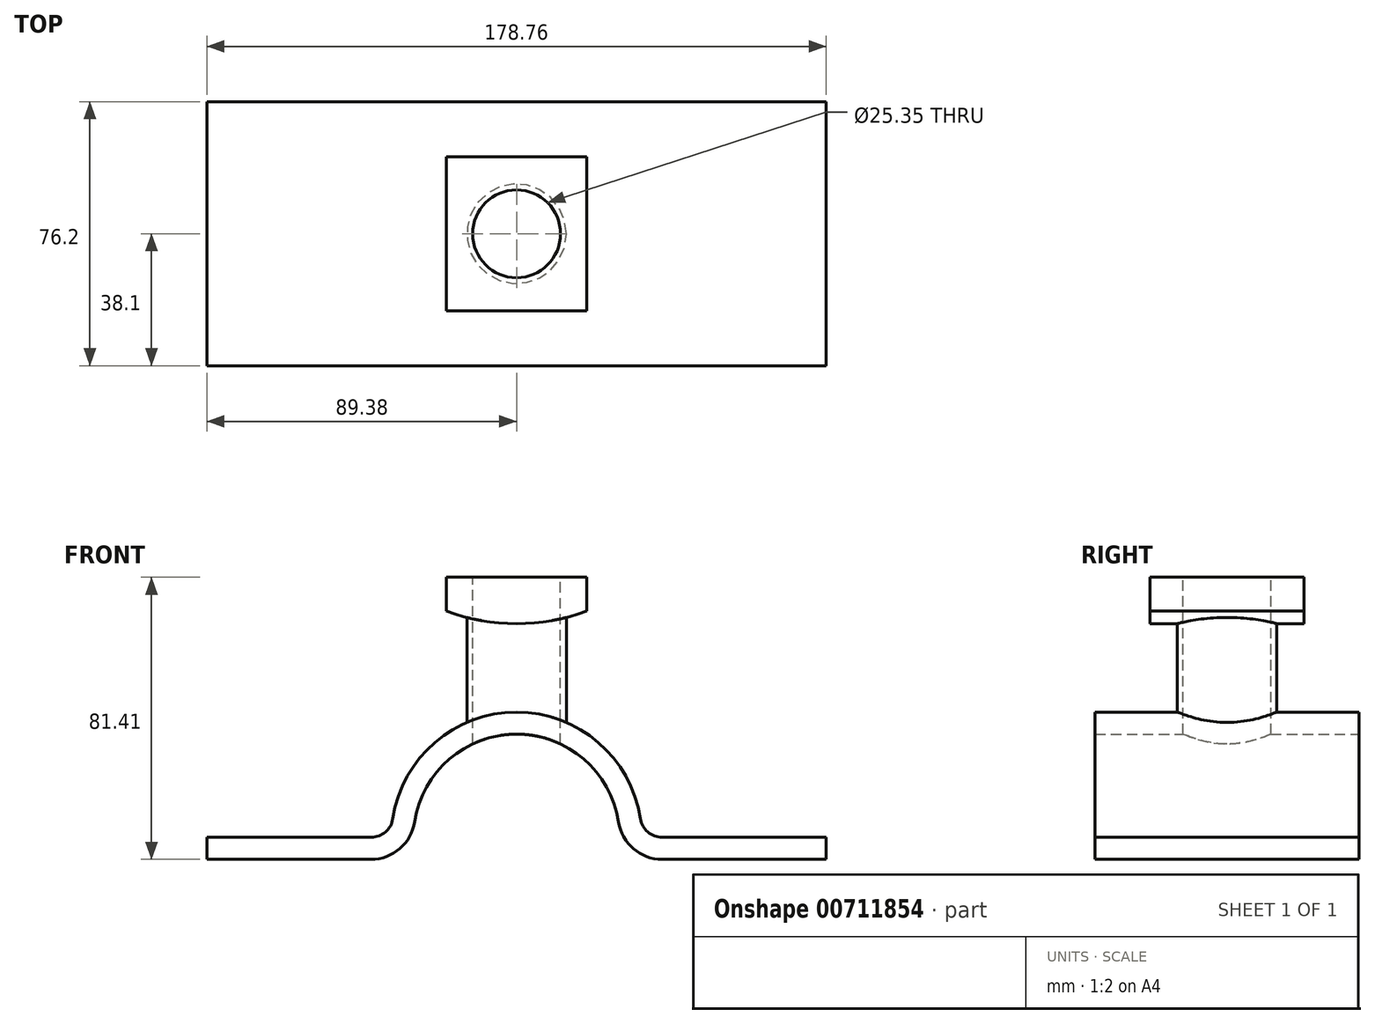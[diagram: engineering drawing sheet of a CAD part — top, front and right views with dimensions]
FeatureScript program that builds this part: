
annotation { "Feature Type Name" : "Feature", "Feature Type Description" : "" }
export const myFeature = defineFeature(function(context is Context, id is Id, definition is map)
    precondition{}
    {
        {
            var Q0;
            Q0=qCreatedBy(makeId("Front.planeOp"),FACE);
            var sketch = newSketch(context, id + "F0", { "sketchPlane" : qUnion([Q0])});
            skArc(sketch, "E0", {"start": v(35.71, 5.4) * mm, "mid": v(0, 36.12) * mm, "end": v(-35.71, 5.4) * mm});
            skLineSegment(sketch, "E1", {"start": v(42, 0) * mm, "end": v(89.38, 0) * mm});
            skLineSegment(sketch, "E2.MirrorCS", {"start": v(-42, 0) * mm, "end": v(-89.38, 0) * mm});
            skPoint(sketch, "E3.visualSharp", {"position": v(-36.12, 0) * mm});
            skArc(sketch, "E3.filletArc", {"start": v(-42, 0) * mm, "mid": v(-37.85, 1.54) * mm, "end": v(-35.71, 5.4) * mm});
            skPoint(sketch, "E4.visualSharp", {"position": v(36.12, 0) * mm});
            skArc(sketch, "E4.filletArc", {"start": v(35.71, 5.4) * mm, "mid": v(37.85, 1.54) * mm, "end": v(42, 0) * mm});
            skLineSegment(sketch, "E5.0", {"start": v(-42, -6.35) * mm, "end": v(-89.38, -6.35) * mm});
            skLineSegment(sketch, "E5.1", {"start": v(42, -6.35) * mm, "end": v(89.38, -6.35) * mm});
            skArc(sketch, "E5.2", {"start": v(29.43, 4.45) * mm, "mid": v(33.7, -3.28) * mm, "end": v(42, -6.35) * mm});
            skArc(sketch, "E5.3", {"start": v(29.43, 4.45) * mm, "mid": v(0, 29.77) * mm, "end": v(-29.43, 4.45) * mm});
            skArc(sketch, "E5.4", {"start": v(-42, -6.35) * mm, "mid": v(-33.7, -3.28) * mm, "end": v(-29.43, 4.45) * mm});
            skLineSegment(sketch, "E6", {"start": v(-89.38, 0) * mm, "end": v(-89.38, -6.35) * mm});
            skLineSegment(sketch, "E7", {"start": v(89.38, 0) * mm, "end": v(89.38, -6.35) * mm});
            skSolve(sketch);
        }
        {
            var Q0;
            Q0=makeQuery(id+"F0.imprint","IMPRINT",FACE,{"disambiguationData":[TD([[makeQuery(id+"F0.imprint","IMPRINT",EDGE,{"derivedFrom":sQuery(id+"F0.wireOp",EDGE,"E0")}),1.0]])]});
            extrude(context, id + "F1", {"entities" : qUnion([Q0]), "endBound" : BoundingType.SYMMETRIC, "depth" : 76.2 * mm, "offsetDistance" : 25.4 * mm});
        }
        {
            var Q0;
            Q0=qCreatedBy(makeId("Front.planeOp"),FACE);
            var sketch = newSketch(context, id + "F2", { "sketchPlane" : qUnion([Q0])});
            skLineSegment(sketch, "E8", {"start": v(0, 0) * mm, "end": v(0, 75.06) * mm, "construction": true});
            skLineSegment(sketch, "E9", {"start": v(0, 75.06) * mm, "end": v(20.2, 75.06) * mm});
            skLineSegment(sketch, "E10", {"start": v(20.2, 75.06) * mm, "end": v(20.2, 65.28) * mm});
            skLineSegment(sketch, "E11.MirrorCS", {"start": v(0, 75.06) * mm, "end": v(-20.2, 75.06) * mm});
            skLineSegment(sketch, "E12.MirrorCS", {"start": v(-20.2, 75.06) * mm, "end": v(-20.2, 65.28) * mm});
            skArc(sketch, "E13", {"start": v(-20.2, 65.28) * mm, "mid": v(0, 61.66) * mm, "end": v(20.2, 65.28) * mm});
            skSolve(sketch);
        }
        {
            var Q0;
            Q0=makeQuery(id+"F2.imprint","IMPRINT",FACE,{"disambiguationData":[TD([[makeQuery(id+"F2.imprint","IMPRINT",EDGE,{"derivedFrom":sQuery(id+"F2.wireOp",EDGE,"E9")}),-1.0]])]});
            extrude(context, id + "F3", {"entities" : qUnion([Q0]), "endBound" : BoundingType.SYMMETRIC, "depth" : 44.45 * mm, "offsetDistance" : 25.4 * mm});
        }
        {
            var Q0;
            Q0=makeQuery(id+"F3.opExtrude","SWEPT_FACE",FACE,{"disambiguationData":[OSD([sQuery(id+"F2.wireOp",EDGE,"E9"),sQuery(id+"F2.wireOp",EDGE,"E11.MirrorCS")])]});
            var sketch = newSketch(context, id + "F4", { "sketchPlane" : qUnion([Q0])});
            skCircle(sketch, "E14", {"center": v(0, 0) * mm, "radius": 14.35 * mm});
            skSolve(sketch);
        }
        {
            var Q0;
            Q0=makeQuery(id+"F4.imprint","IMPRINT",FACE,{"disambiguationData":[TD([[makeQuery(id+"F4.imprint","IMPRINT",EDGE,{"derivedFrom":sQuery(id+"F4.wireOp",EDGE,"e410480c-99a0-46d0-b2d6-22db8fb7545a.0")}),1.0]])]});
            var Q1;
            Q1=makeQuery(id+"F4.imprint","IMPRINT",FACE,{"disambiguationData":[TD([[makeQuery(id+"F4.imprint","IMPRINT",EDGE,{"derivedFrom":sQuery(id+"F4.wireOp",EDGE,"E14")}),1.0]])]});
            var Q2;
            Q2=makeQuery(id+"F1.opExtrude","SWEPT_FACE",FACE,{"disambiguationData":[OSD([sQuery(id+"F0.wireOp",EDGE,"E0")])]});
            extrude(context, id + "F5", {"entities" : qUnion([Q0, Q1]), "operationType" : NewBodyOperationType.ADD, "endBound" : BoundingType.UP_TO_SURFACE, "oppositeDirection" : true, "depth" : 25.4 * mm, "endBoundEntityFace" : qUnion([Q2]), "offsetDistance" : 25.4 * mm});
        }
        {
            var Q0;
            Q0=makeQuery(id+"F3.opExtrude","SWEPT_FACE",FACE,{"disambiguationData":[OSD([sQuery(id+"F2.wireOp",EDGE,"E9"),sQuery(id+"F2.wireOp",EDGE,"E11.MirrorCS")])]});
            var sketch = newSketch(context, id + "F6", { "sketchPlane" : qUnion([Q0])});
            skCircle(sketch, "E15", {"center": v(0, 0) * mm, "radius": 12.67 * mm});
            skSolve(sketch);
        }
        {
            var Q0;
            Q0 = qSketchRegion(id + "F6", true);
            extrude(context, id + "F7", {"entities" : qUnion([Q0]), "operationType" : NewBodyOperationType.REMOVE, "endBound" : BoundingType.THROUGH_ALL, "oppositeDirection" : true, "depth" : 25.4 * mm, "offsetDistance" : 25.4 * mm});
        }
    });
